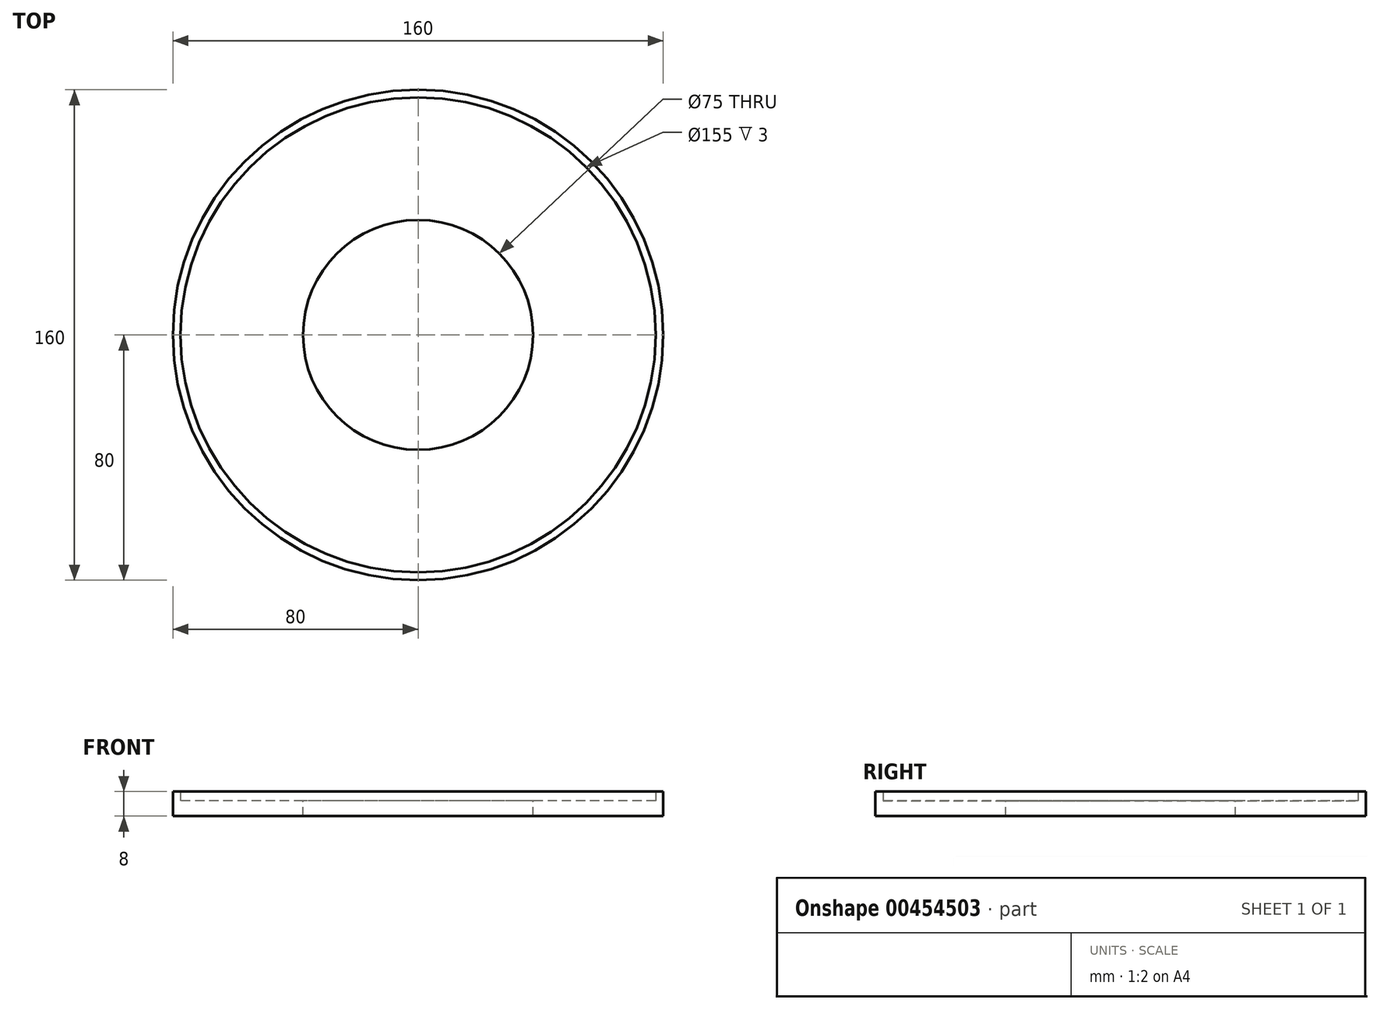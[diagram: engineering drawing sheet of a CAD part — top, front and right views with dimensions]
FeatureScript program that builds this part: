
annotation { "Feature Type Name" : "Feature", "Feature Type Description" : "" }
export const myFeature = defineFeature(function(context is Context, id is Id, definition is map)
    precondition{}
    {
        {
            var Q0;
            Q0=qCreatedBy(makeId("Top.planeOp"),FACE);
            var sketch = newSketch(context, id + "F0", { "sketchPlane" : qUnion([Q0])});
            skCircle(sketch, "E0", {"center": v(0, 0) * mm, "radius": 80 * mm});
            skSolve(sketch);
        }
        {
            var Q0;
            Q0=makeQuery(id+"F0.imprint","IMPRINT",FACE,{"disambiguationData":[TD([[makeQuery(id+"F0.imprint","IMPRINT",EDGE,{"derivedFrom":sQuery(id+"F0.wireOp",EDGE,"E0")}),1.0]])]});
            extrude(context, id + "F1", {"entities" : qUnion([Q0]), "depth" : 5 * mm});
        }
        {
            var Q0;
            Q0=makeQuery(id+"F1.opExtrude","CAP_FACE",FACE,{"disambiguationData":[OSD([sQuery(id+"F0.wireOp",EDGE,"E0")])],"isStart":false});
            var sketch = newSketch(context, id + "F2", { "sketchPlane" : qUnion([Q0])});
            skCircle(sketch, "E1", {"center": v(0, 0) * mm, "radius": 37.5 * mm});
            skSolve(sketch);
        }
        {
            var Q0;
            Q0 = qSketchRegion(id + "F2", true);
            extrude(context, id + "F3", {"entities" : qUnion([Q0]), "operationType" : NewBodyOperationType.REMOVE, "endBound" : BoundingType.THROUGH_ALL, "oppositeDirection" : true, "depth" : 25 * mm});
        }
        {
            var Q0;
            Q0=makeQuery(id+"F1.opExtrude","CAP_FACE",FACE,{"disambiguationData":[OSD([sQuery(id+"F0.wireOp",EDGE,"E0")])],"isStart":false});
            var sketch = newSketch(context, id + "F4", { "sketchPlane" : qUnion([Q0])});
            skCircle(sketch, "E2", {"center": v(0, 0) * mm, "radius": 80 * mm});
            skCircle(sketch, "E3", {"center": v(0, 0) * mm, "radius": 77.5 * mm});
            skSolve(sketch);
        }
        {
            var Q0;
            Q0=makeQuery(id+"F4.imprint","IMPRINT",FACE,{"disambiguationData":[TD([[makeQuery(id+"F4.imprint","IMPRINT",EDGE,{"derivedFrom":sQuery(id+"F4.wireOp",EDGE,"E2")}),1.0]])]});
            extrude(context, id + "F5", {"entities" : qUnion([Q0]), "operationType" : NewBodyOperationType.ADD, "depth" : 3 * mm});
        }
    });
